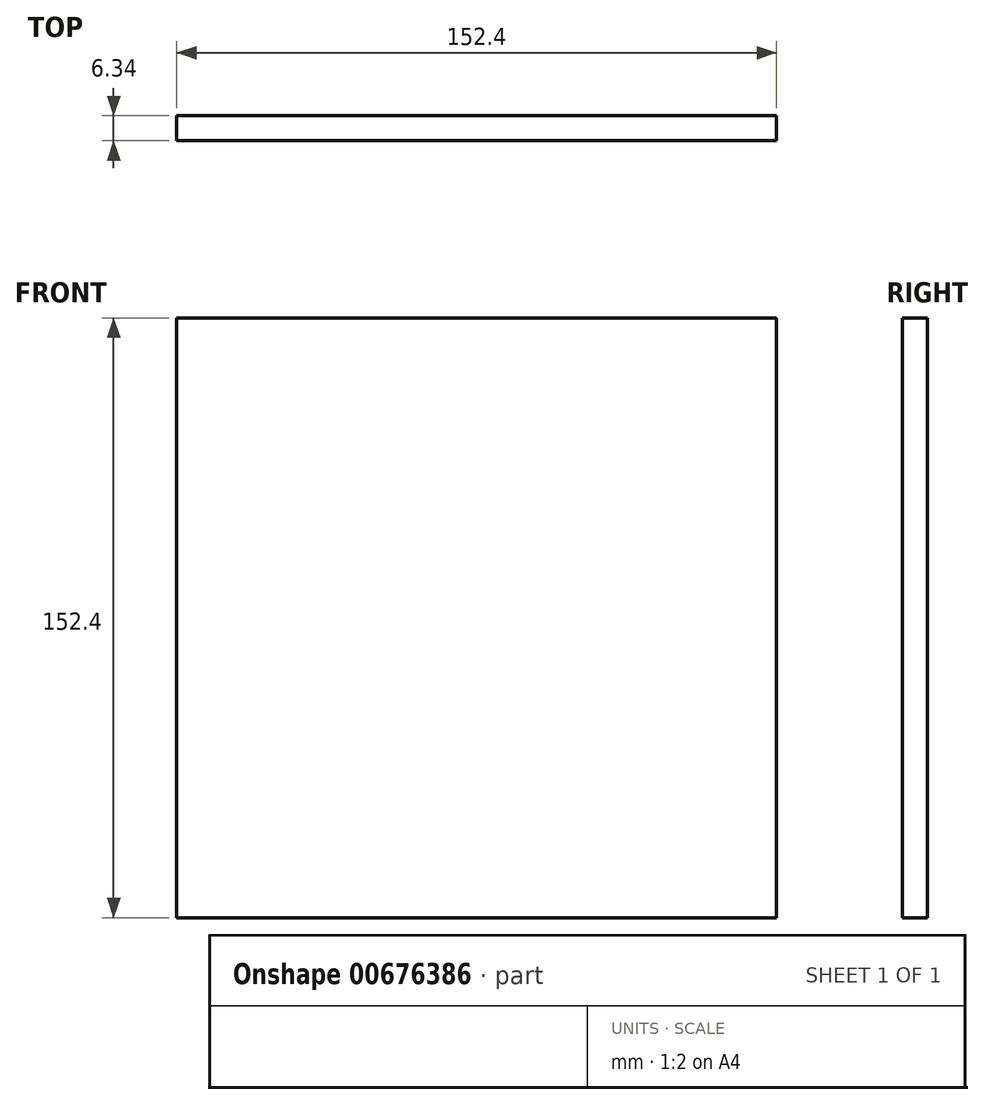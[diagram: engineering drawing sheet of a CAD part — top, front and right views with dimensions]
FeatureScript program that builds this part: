
annotation { "Feature Type Name" : "Feature", "Feature Type Description" : "" }
export const myFeature = defineFeature(function(context is Context, id is Id, definition is map)
    precondition{}
    {
        {
            var Q0;
            Q0=qCreatedBy(makeId("Front.planeOp"),FACE);
            var sketch = newSketch(context, id + "F0", { "sketchPlane" : qUnion([Q0])});
            skLineSegment(sketch, "E0.bottom", {"start": v(-76.2, 76.2) * mm, "end": v(76.2, 76.2) * mm});
            skLineSegment(sketch, "E0.top", {"start": v(-76.2, -76.2) * mm, "end": v(76.2, -76.2) * mm});
            skLineSegment(sketch, "E0.left", {"start": v(-76.2, 76.2) * mm, "end": v(-76.2, -76.2) * mm});
            skLineSegment(sketch, "E0.right", {"start": v(76.2, 76.2) * mm, "end": v(76.2, -76.2) * mm});
            skPoint(sketch, "E0.middle", {"position": v(0, 0) * mm});
            skSolve(sketch);
        }
        {
            var Q0;
            Q0=makeQuery(id+"F0.imprint","IMPRINT",FACE,{"disambiguationData":[TD([[makeQuery(id+"F0.imprint","IMPRINT",EDGE,{"derivedFrom":sQuery(id+"F0.wireOp",EDGE,"E0.bottom")}),-1.0]])]});
            extrude(context, id + "F1", {"entities" : qUnion([Q0]), "endBound" : BoundingType.SYMMETRIC, "depth" : 6.35 * mm, "offsetDistance" : 25.4 * mm});
        }
    });
